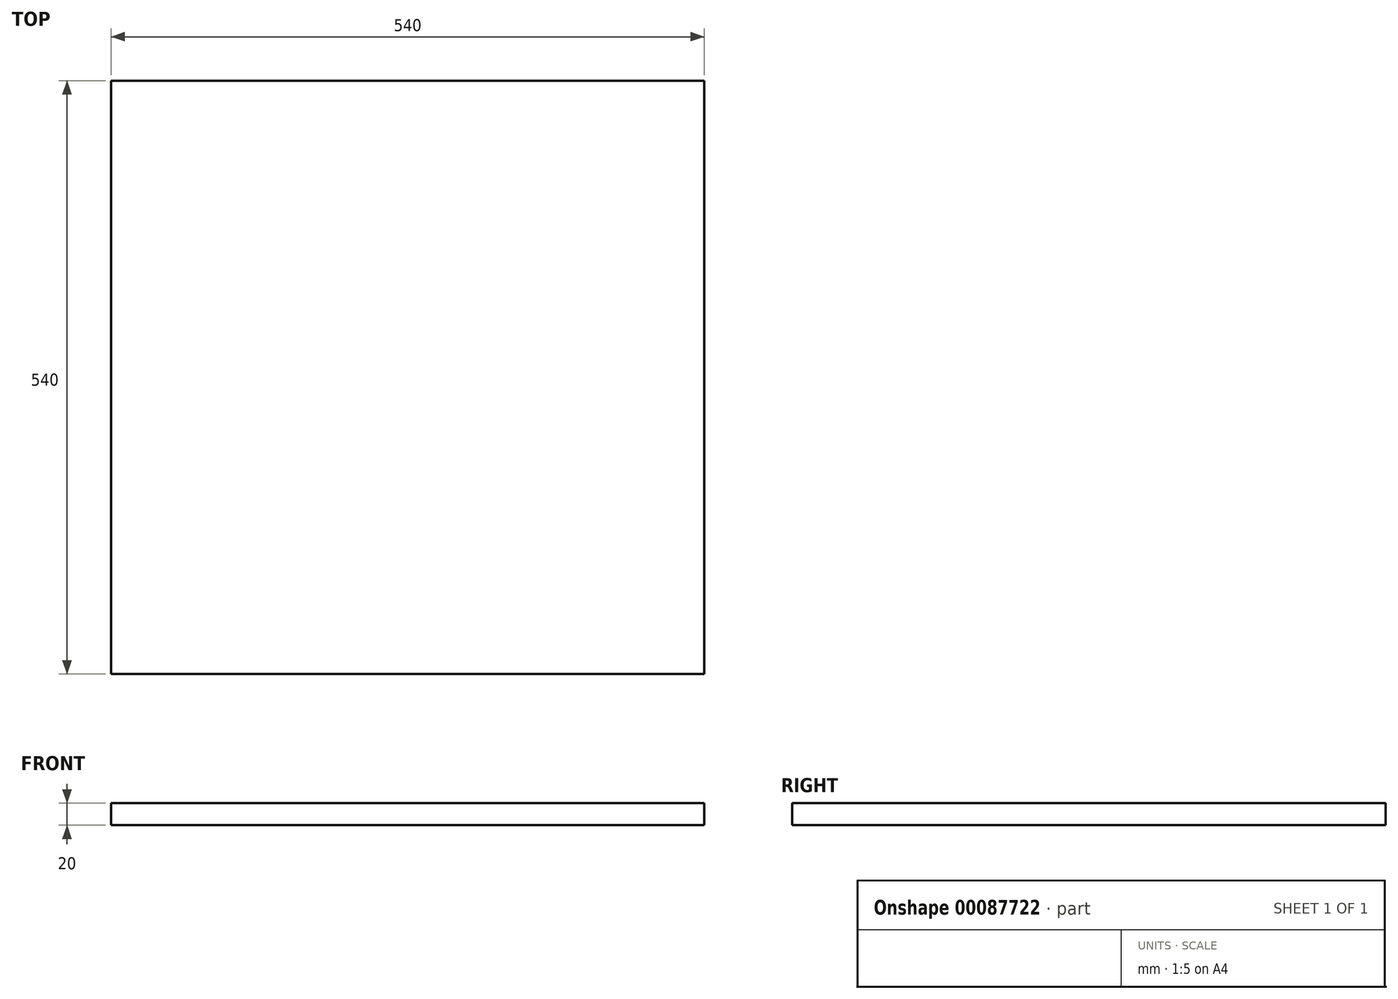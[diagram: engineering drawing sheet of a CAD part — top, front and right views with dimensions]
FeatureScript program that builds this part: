
annotation { "Feature Type Name" : "Feature", "Feature Type Description" : "" }
export const myFeature = defineFeature(function(context is Context, id is Id, definition is map)
    precondition{}
    {
        {
            var Q0;
            Q0=qCreatedBy(makeId("Top.planeOp"),FACE);
            var sketch = newSketch(context, id + "F0", { "sketchPlane" : qUnion([Q0])});
            skLineSegment(sketch, "E0.bottom", {"start": v(0, 0) * mm, "end": v(540, 0) * mm});
            skLineSegment(sketch, "E0.top", {"start": v(0, 540) * mm, "end": v(540, 540) * mm});
            skLineSegment(sketch, "E0.left", {"start": v(0, 0) * mm, "end": v(0, 540) * mm});
            skLineSegment(sketch, "E0.right", {"start": v(540, 0) * mm, "end": v(540, 540) * mm});
            skSolve(sketch);
        }
        {
            var Q0;
            Q0=makeQuery(id+"F0.imprint","IMPRINT",FACE,{"disambiguationData":[TD([[makeQuery(id+"F0.imprint","IMPRINT",EDGE,{"derivedFrom":sQuery(id+"F0.wireOp",EDGE,"E0.bottom")}),1.0]])]});
            extrude(context, id + "F1", {"entities" : qUnion([Q0]), "depth" : 20 * mm});
        }
    });
